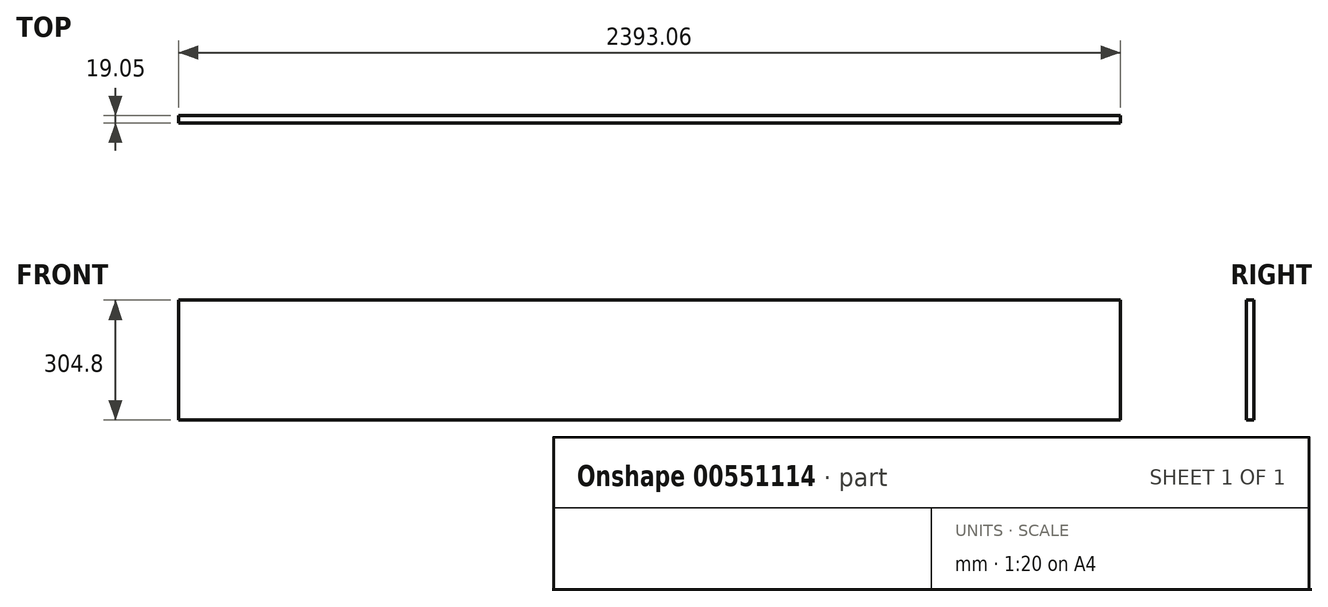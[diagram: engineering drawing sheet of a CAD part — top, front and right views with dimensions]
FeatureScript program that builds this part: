
annotation { "Feature Type Name" : "Feature", "Feature Type Description" : "" }
export const myFeature = defineFeature(function(context is Context, id is Id, definition is map)
    precondition{}
    {
        {
            var Q0;
            Q0=qCreatedBy(makeId("Front.planeOp"),FACE);
            var sketch = newSketch(context, id + "F0", { "sketchPlane" : qUnion([Q0])});
            skLineSegment(sketch, "E0.bottom", {"start": v(1196.53, 152.4) * mm, "end": v(-1196.53, 152.4) * mm});
            skLineSegment(sketch, "E0.top", {"start": v(1196.53, -152.4) * mm, "end": v(-1196.53, -152.4) * mm});
            skLineSegment(sketch, "E0.left", {"start": v(1196.53, 152.4) * mm, "end": v(1196.53, -152.4) * mm});
            skLineSegment(sketch, "E0.right", {"start": v(-1196.53, 152.4) * mm, "end": v(-1196.53, -152.4) * mm});
            skPoint(sketch, "E0.middle", {"position": v(0, 0) * mm});
            skSolve(sketch);
        }
        {
            var Q0;
            Q0=makeQuery(id+"F0.imprint","IMPRINT",FACE,{"disambiguationData":[TD([[makeQuery(id+"F0.imprint","IMPRINT",EDGE,{"derivedFrom":sQuery(id+"F0.wireOp",EDGE,"E0.bottom")}),1.0]])]});
            extrude(context, id + "F1", {"entities" : qUnion([Q0]), "depth" : 19.05 * mm, "offsetDistance" : 25.4 * mm});
        }
    });
